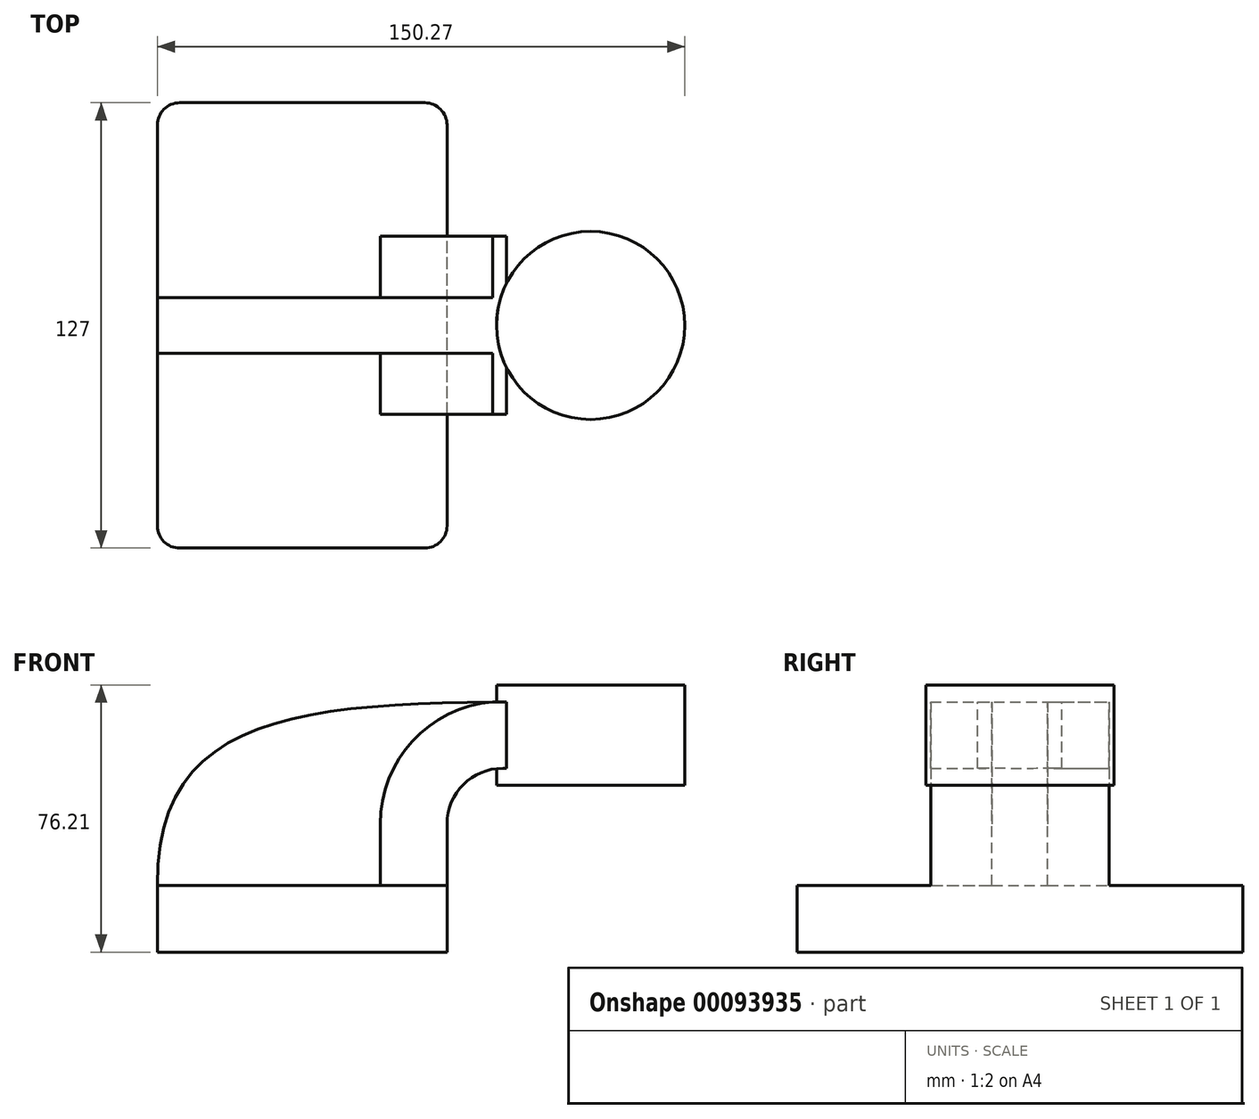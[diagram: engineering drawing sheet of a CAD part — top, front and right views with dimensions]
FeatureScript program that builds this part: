
annotation { "Feature Type Name" : "Feature", "Feature Type Description" : "" }
export const myFeature = defineFeature(function(context is Context, id is Id, definition is map)
    precondition{}
    {
        {
            var Q0;
            Q0=qCreatedBy(makeId("Front.planeOp"),FACE);
            var sketch = newSketch(context, id + "F0", { "sketchPlane" : qUnion([Q0])});
            skLineSegment(sketch, "E0.bottom", {"start": v(41.28, -9.52) * mm, "end": v(-41.27, -9.52) * mm});
            skLineSegment(sketch, "E0.top", {"start": v(41.27, 9.53) * mm, "end": v(-41.27, 9.53) * mm});
            skLineSegment(sketch, "E0.left", {"start": v(41.28, -9.52) * mm, "end": v(41.28, 9.53) * mm});
            skLineSegment(sketch, "E0.right", {"start": v(-41.27, -9.52) * mm, "end": v(-41.27, 9.53) * mm});
            skPoint(sketch, "E0.middle", {"position": v(0, 0) * mm});
            skLineSegment(sketch, "E1.bottom", {"start": v(108.99, 38.1) * mm, "end": v(58.19, 38.1) * mm});
            skLineSegment(sketch, "E1.top", {"start": v(108.99, 66.68) * mm, "end": v(58.19, 66.68) * mm});
            skLineSegment(sketch, "E1.left", {"start": v(108.99, 38.1) * mm, "end": v(108.99, 66.67) * mm});
            skLineSegment(sketch, "E1.right", {"start": v(58.19, 38.1) * mm, "end": v(58.19, 66.67) * mm});
            skPoint(sketch, "E1.middle", {"position": v(83.59, 52.39) * mm});
            skLineSegment(sketch, "E2", {"start": v(41.27, 9.53) * mm, "end": v(41.27, 27) * mm});
            skArc(sketch, "E3", {"start": v(41.27, 27) * mm, "mid": v(45.92, 38.23) * mm, "end": v(57.15, 42.88) * mm});
            skLineSegment(sketch, "E4", {"start": v(57.15, 42.88) * mm, "end": v(85.72, 42.88) * mm});
            skArc(sketch, "E5.0", {"start": v(22.22, 27) * mm, "mid": v(33.25, 52.47) * mm, "end": v(59.36, 61.86) * mm});
            skLineSegment(sketch, "E5.1", {"start": v(22.22, 9.53) * mm, "end": v(22.22, 27) * mm});
            skLineSegment(sketch, "E6", {"start": v(59.36, 61.86) * mm, "end": v(84.64, 61.86) * mm});
            skFitSpline(sketch, "E7", {"points": [v(-41.28, 9.53) * mm, v(59.36, 61.86) * mm], "startDerivative": vector(-1.59, 145.75) * mm, "endDerivative": vector(178.08, 1.3) * mm});
            skLineSegment(sketch, "E8", {"start": v(82.17, 78.58) * mm, "end": v(82.17, 24.2) * mm});
            skSolve(sketch);
        }
        {
            var Q0;
            Q0=makeQuery(id+"F0.imprint","IMPRINT",FACE,{"disambiguationData":[TD([[makeQuery(id+"F0.imprint","IMPRINT",EDGE,{"derivedFrom":sQuery(id+"F0.wireOp",EDGE,"E0.bottom")}),-1.0]])]});
            extrude(context, id + "F1", {"entities" : qUnion([Q0]), "endBound" : BoundingType.SYMMETRIC, "depth" : 127 * mm});
        }
        {
            var Q0;
            {var subQ1=sQuery(id+"F0.wireOp",EDGE,"E2");Q0=makeQuery(id+"F0.imprint","IMPRINT",FACE,{"disambiguationData":[TD([[makeQuery(id+"F0.imprint","IMPRINT",EDGE,{"derivedFrom":subQ1}),1.0]])]});}
            extrude(context, id + "F2", {"entities" : qUnion([Q0]), "operationType" : NewBodyOperationType.ADD, "endBound" : BoundingType.SYMMETRIC, "depth" : 50.8 * mm});
        }
        {
            var Q0;
            {var subQ3=sQuery(id+"F0.wireOp",EDGE,"E5.1");Q0=makeQuery(id+"F0.imprint","IMPRINT",FACE,{"disambiguationData":[TD([[makeQuery(id+"F0.imprint","IMPRINT",EDGE,{"derivedFrom":subQ3}),1.0]])]});}
            extrude(context, id + "F3", {"entities" : qUnion([Q0]), "operationType" : NewBodyOperationType.ADD, "endBound" : BoundingType.SYMMETRIC, "depth" : 15.88 * mm});
        }
        {
            var Q0;
            {var subQ4=sQuery(id+"F0.wireOp",EDGE,"E1.left");Q0=makeQuery(id+"F0.imprint","IMPRINT",FACE,{"disambiguationData":[TD([[makeQuery(id+"F0.imprint","IMPRINT",EDGE,{"derivedFrom":subQ4}),1.0]])]});}
            var Q1;
            Q1=sQuery(id+"F0.wireOp",EDGE,"E8");
            revolve(context, id + "F4", {"operationType" : NewBodyOperationType.ADD, "entities" : qUnion([Q0]), "axis" : qUnion([Q1]), "revolveType" : RevolveType.FULL});
        }
        {
            var Q0;
            Q0=makeQuery(id+"F1.opExtrude","CAP_EDGE",EDGE,{"disambiguationData":[OSD([sQuery(id+"F0.wireOp",EDGE,"E0.left")])],"isStart":false});
            var Q1;
            Q1=makeQuery(id+"F1.opExtrude","CAP_EDGE",EDGE,{"disambiguationData":[OSD([sQuery(id+"F0.wireOp",EDGE,"E0.right")])],"isStart":false});
            var Q2;
            Q2=makeQuery(id+"F1.opExtrude","CAP_EDGE",EDGE,{"disambiguationData":[OSD([sQuery(id+"F0.wireOp",EDGE,"E0.left")])],"isStart":true});
            var Q3;
            Q3=makeQuery(id+"F1.opExtrude","CAP_EDGE",EDGE,{"disambiguationData":[OSD([sQuery(id+"F0.wireOp",EDGE,"E0.right")])],"isStart":true});
            fillet(context, id + "F5", {"entities" : qUnion([Q0, Q1, Q2, Q3]), "radius" : 6.35 * mm, "tangentPropagation" : true, "allowEdgeOverflow" : false});
        }
    });
